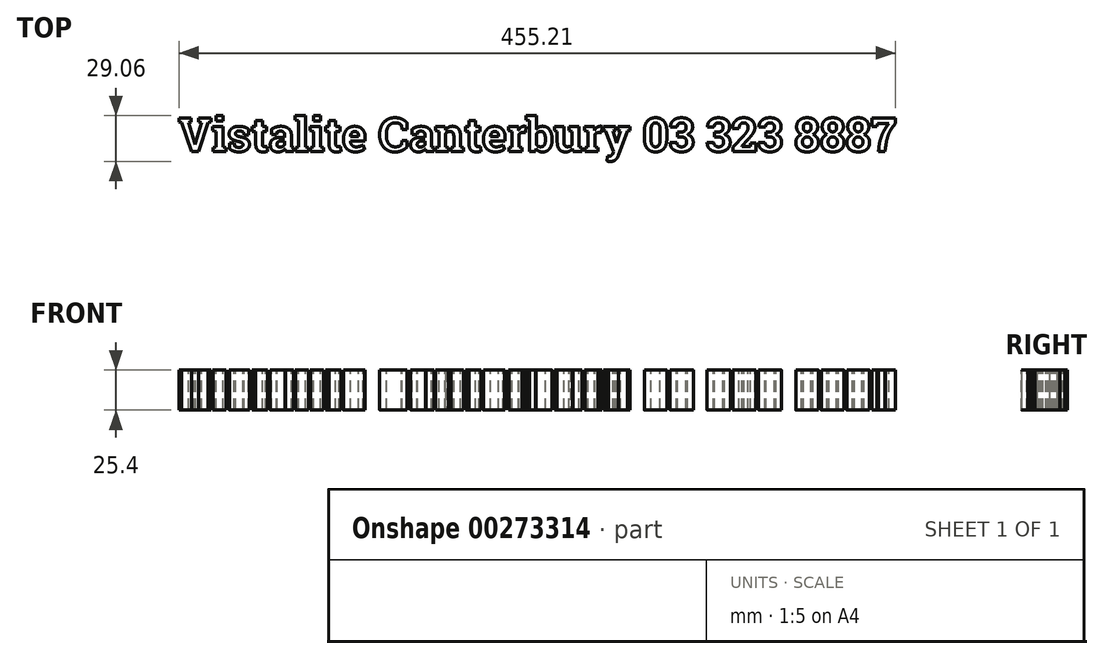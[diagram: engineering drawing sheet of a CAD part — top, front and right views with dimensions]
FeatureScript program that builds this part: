
annotation { "Feature Type Name" : "Feature", "Feature Type Description" : "" }
export const myFeature = defineFeature(function(context is Context, id is Id, definition is map)
    precondition{}
    {
        {
            var Q0;
            Q0=qCreatedBy(makeId("Top.planeOp"),FACE);
            var sketch = newSketch(context, id + "F0", { "sketchPlane" : qUnion([Q0])});
            skText(sketch, "E0", { "text": "Vistalite Canterbury 03 323 8887", "fontName": "RobotoSlab-Bold.ttf"});
            const initialGuessF0  = {"E0": [-0.24758, 0.00063, 1, 0, 0.02146]};
            skSetInitialGuess(sketch, initialGuessF0);
            skSolve(sketch);
        }
        {
            var Q0;
            Q0 = qConstructionFilter(qBodyType(qCreatedBy(id + "F0" ,EDGE), BodyType.WIRE), ConstructionObject.NO);
            extrude(context, id + "F1", {"bodyType" : ToolBodyType.SURFACE, "surfaceEntities" : qUnion([Q0]), "depth" : 25.4 * mm});
        }
    });
